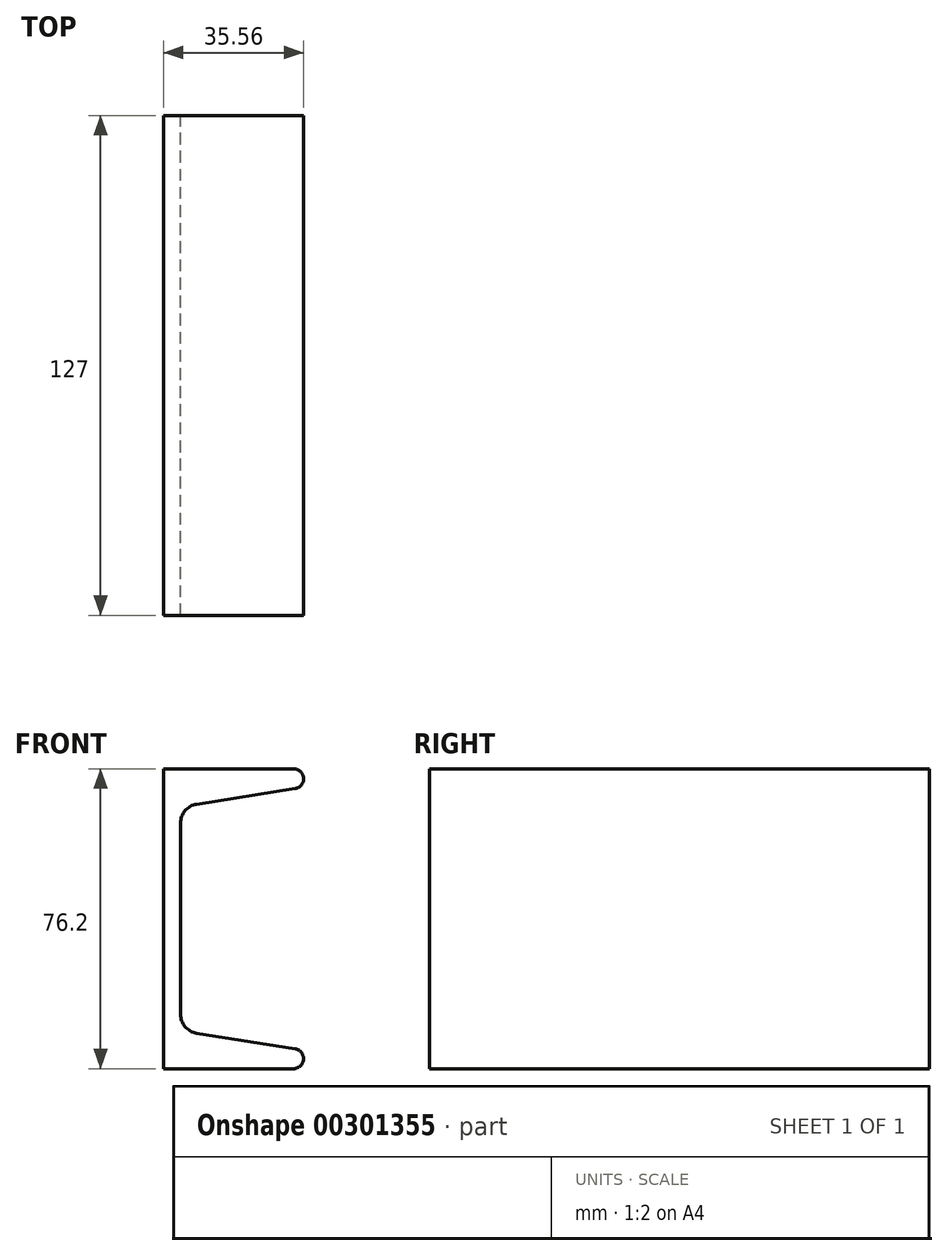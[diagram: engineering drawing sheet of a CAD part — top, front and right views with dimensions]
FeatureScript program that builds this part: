
annotation { "Feature Type Name" : "Feature", "Feature Type Description" : "" }
export const myFeature = defineFeature(function(context is Context, id is Id, definition is map)
    precondition{}
    {
        {
            var Q0;
            Q0=qCreatedBy(makeId("Front.planeOp"),FACE);
            var sketch = newSketch(context, id + "F0", { "sketchPlane" : qUnion([Q0])});
            skLineSegment(sketch, "E0", {"start": v(0, 0) * mm, "end": v(0, 38.1) * mm});
            skLineSegment(sketch, "E1", {"start": v(0, 38.1) * mm, "end": v(33.02, 38.1) * mm});
            skArc(sketch, "E2", {"start": v(33.02, 38.1) * mm, "mid": v(35.55, 35.76) * mm, "end": v(33.42, 33.05) * mm});
            skLineSegment(sketch, "E3", {"start": v(33.42, 33.05) * mm, "end": v(8.41, 29.1) * mm});
            skLineSegment(sketch, "E4", {"start": v(4.32, 24.3) * mm, "end": v(4.32, 0) * mm});
            skPoint(sketch, "E5.visualSharp", {"position": v(4.32, 28.44) * mm});
            skArc(sketch, "E5.filletArc", {"start": v(8.41, 29.1) * mm, "mid": v(5.48, 27.45) * mm, "end": v(4.32, 24.3) * mm});
            skArc(sketch, "E6.MirrorCS", {"start": v(8.41, -29.1) * mm, "mid": v(5.48, -27.45) * mm, "end": v(4.32, -24.3) * mm});
            skLineSegment(sketch, "E7.MirrorCS", {"start": v(0, 0) * mm, "end": v(0, -38.1) * mm});
            skLineSegment(sketch, "E8.MirrorCS", {"start": v(4.32, -24.3) * mm, "end": v(4.32, 0) * mm});
            skPoint(sketch, "E9.MirrorP", {"position": v(4.32, -28.44) * mm});
            skLineSegment(sketch, "E10.MirrorCS", {"start": v(0, -38.1) * mm, "end": v(33.02, -38.1) * mm});
            skLineSegment(sketch, "E11.MirrorCS", {"start": v(33.42, -33.05) * mm, "end": v(8.41, -29.1) * mm});
            skArc(sketch, "E12.MirrorCS", {"start": v(33.02, -38.1) * mm, "mid": v(35.55, -35.76) * mm, "end": v(33.42, -33.05) * mm});
            skSolve(sketch);
        }
        {
            var Q0;
            Q0=makeQuery(id+"F0.imprint","IMPRINT",FACE,{"disambiguationData":[TD([[makeQuery(id+"F0.imprint","IMPRINT",EDGE,{"derivedFrom":sQuery(id+"F0.wireOp",EDGE,"E0")}),-1.0]])]});
            extrude(context, id + "F1", {"entities" : qUnion([Q0]), "depth" : 127 * mm});
        }
    });
